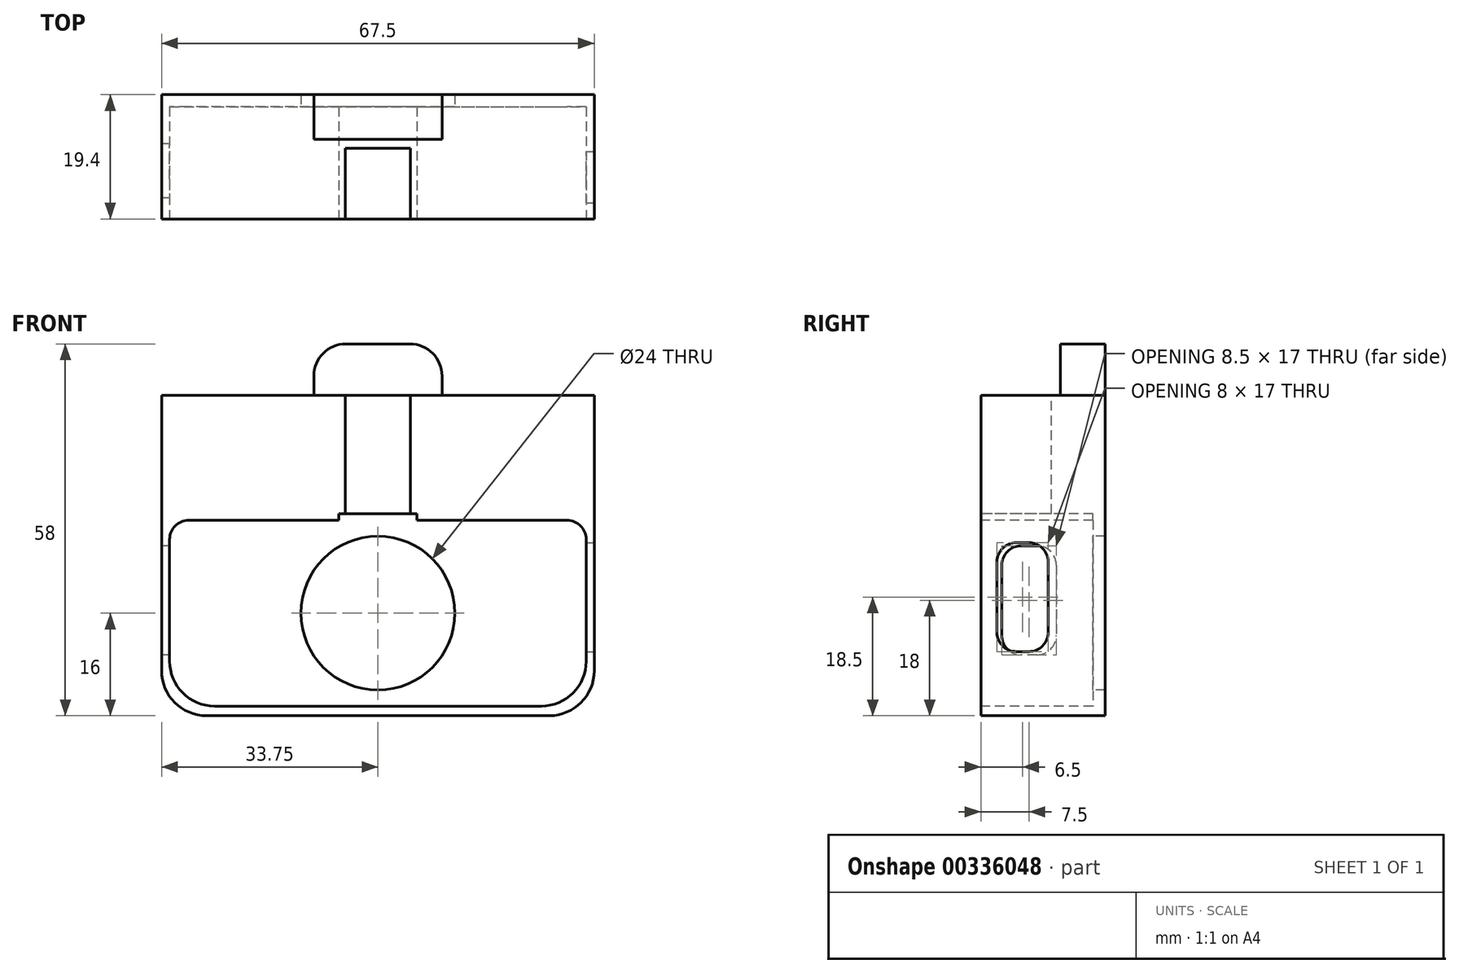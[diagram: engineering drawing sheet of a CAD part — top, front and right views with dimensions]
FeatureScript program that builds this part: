
annotation { "Feature Type Name" : "Feature", "Feature Type Description" : "" }
export const myFeature = defineFeature(function(context is Context, id is Id, definition is map)
    precondition{}
    {
        {
            var Q0;
            Q0=qCreatedBy(makeId("Top.planeOp"),FACE);
            var sketch = newSketch(context, id + "F0", { "sketchPlane" : qUnion([Q0])});
            skLineSegment(sketch, "E0.bottom", {"start": v(-33.75, 9.7) * mm, "end": v(33.75, 9.7) * mm});
            skLineSegment(sketch, "E0.top", {"start": v(-33.75, -9.7) * mm, "end": v(33.75, -9.7) * mm});
            skLineSegment(sketch, "E0.left", {"start": v(-33.75, 9.7) * mm, "end": v(-33.75, -9.7) * mm});
            skLineSegment(sketch, "E0.right", {"start": v(33.75, 9.7) * mm, "end": v(33.75, -9.7) * mm});
            skPoint(sketch, "E0.middle", {"position": v(0, 0) * mm});
            skSolve(sketch);
        }
        {
            var Q0;
            Q0=makeQuery(id+"F0.imprint","IMPRINT",FACE,{"disambiguationData":[TD([[makeQuery(id+"F0.imprint","IMPRINT",EDGE,{"derivedFrom":sQuery(id+"F0.wireOp",EDGE,"E0.bottom")}),-1.0]])]});
            extrude(context, id + "F1", {"entities" : qUnion([Q0]), "flatOperationType" : FlatOperationType.REMOVE, "offsetDistance" : 25 * mm, "depth" : 50 * mm, "domain" : OperationDomain.MODEL});
        }
        {
            var Q0;
            Q0=makeQuery(id+"F1.opExtrude","SWEPT_FACE",FACE,{"disambiguationData":[OSD([sQuery(id+"F0.wireOp",EDGE,"E0.top")])]});
            var sketch = newSketch(context, id + "F2", { "sketchPlane" : qUnion([Q0])});
            skLineSegment(sketch, "E1", {"start": v(-6.1, 30.5) * mm, "end": v(-29.5, 30.5) * mm});
            skLineSegment(sketch, "E2", {"start": v(-32.5, 27.5) * mm, "end": v(-32.5, 1.5) * mm});
            skLineSegment(sketch, "E3", {"start": v(-32.5, 1.5) * mm, "end": v(0, 1.5) * mm});
            skLineSegment(sketch, "E4.MirrorCS", {"start": v(6.1, 30.5) * mm, "end": v(29.5, 30.5) * mm});
            skLineSegment(sketch, "E5.MirrorCS", {"start": v(32.5, 27.5) * mm, "end": v(32.5, 1.5) * mm});
            skLineSegment(sketch, "E6.MirrorCS", {"start": v(32.5, 1.5) * mm, "end": v(0, 1.5) * mm});
            skPoint(sketch, "E7.visualSharp", {"position": v(-32.5, 30.5) * mm});
            skArc(sketch, "E7.filletArc", {"start": v(-29.5, 30.5) * mm, "mid": v(-31.62, 29.62) * mm, "end": v(-32.5, 27.5) * mm});
            skPoint(sketch, "E8.visualSharp", {"position": v(32.5, 30.5) * mm});
            skArc(sketch, "E8.filletArc", {"start": v(32.5, 27.5) * mm, "mid": v(31.62, 29.62) * mm, "end": v(29.5, 30.5) * mm});
            skLineSegment(sketch, "E9", {"start": v(-6.1, 30.5) * mm, "end": v(-6.1, 31.5) * mm});
            skLineSegment(sketch, "E10", {"start": v(-6.1, 31.5) * mm, "end": v(0, 31.5) * mm});
            skLineSegment(sketch, "E11.MirrorCS", {"start": v(6.1, 31.5) * mm, "end": v(0, 31.5) * mm});
            skLineSegment(sketch, "E12.MirrorCS", {"start": v(6.1, 30.5) * mm, "end": v(6.1, 31.5) * mm});
            skLineSegment(sketch, "E13", {"start": v(-5.1, 31.5) * mm, "end": v(-5.1, 50) * mm});
            skLineSegment(sketch, "E14", {"start": v(-5.1, 50) * mm, "end": v(0, 50) * mm});
            skLineSegment(sketch, "E15.MirrorCS", {"start": v(5.1, 50) * mm, "end": v(0, 50) * mm});
            skLineSegment(sketch, "E16.MirrorCS", {"start": v(5.1, 31.5) * mm, "end": v(5.1, 50) * mm});
            skSolve(sketch);
        }
        {
            var Q0;
            Q0=makeQuery(id+"F2.imprint","IMPRINT",FACE,{"disambiguationData":[TD([[makeQuery(id+"F2.imprint","IMPRINT",EDGE,{"derivedFrom":sQuery(id+"F2.wireOp",EDGE,"E1")}),1.0]])]});
            extrude(context, id + "F3", {"entities" : qUnion([Q0]), "operationType" : NewBodyOperationType.REMOVE, "flatOperationType" : FlatOperationType.REMOVE, "oppositeDirection" : true, "offsetDistance" : 25 * mm, "depth" : 17.5 * mm, "domain" : OperationDomain.MODEL});
        }
        {
            var Q0;
            Q0=makeQuery(id+"F3.boolean.opBoolean","COPY",FACE,{"derivedFrom":makeQuery(id+"F3.opExtrude","CAP_FACE",FACE,{"disambiguationData":[OSD([sQuery(id+"F2.wireOp",EDGE,"TUqootcI-8BxO-Xh3T-3ziC-AMeacjTwoGFO"),sQuery(id+"F2.wireOp",EDGE,"E1"),sQuery(id+"F2.wireOp",EDGE,"E2"),sQuery(id+"F2.wireOp",EDGE,"E3"),sQuery(id+"F2.wireOp",EDGE,"TnrEAHaC-nVOl-LSU4-eOLw-rkPotzCDHw9t"),sQuery(id+"F2.wireOp",EDGE,"8e3f61eb-42e3-43cc-a17b-0ce0254c29820.MirrorCS"),sQuery(id+"F2.wireOp",EDGE,"b324ff84-6e96-4d2f-b36d-c2ef43af87640.MirrorCS"),sQuery(id+"F2.wireOp",EDGE,"E4.MirrorCS"),sQuery(id+"F2.wireOp",EDGE,"E5.MirrorCS"),sQuery(id+"F2.wireOp",EDGE,"E6.MirrorCS")])],"isStart":false})});
            var sketch = newSketch(context, id + "F4", { "sketchPlane" : qUnion([Q0])});
            skCircle(sketch, "E17", {"center": v(0, 16) * mm, "radius": 12 * mm});
            skSolve(sketch);
        }
        {
            var Q0;
            Q0=makeQuery(id+"F4.imprint","IMPRINT",FACE,{"disambiguationData":[TD([[makeQuery(id+"F4.imprint","IMPRINT",EDGE,{"derivedFrom":sQuery(id+"F4.wireOp",EDGE,"E17")}),1.0]])]});
            extrude(context, id + "F5", {"entities" : qUnion([Q0]), "operationType" : NewBodyOperationType.REMOVE, "flatOperationType" : FlatOperationType.REMOVE, "endBound" : BoundingType.UP_TO_NEXT, "oppositeDirection" : true, "offsetDistance" : 25 * mm, "depth" : 25 * mm, "domain" : OperationDomain.MODEL});
        }
        {
            var Q0;
            Q0=makeQuery(id+"F1.opExtrude","SWEPT_FACE",FACE,{"disambiguationData":[OSD([sQuery(id+"F0.wireOp",EDGE,"E0.left")])]});
            var sketch = newSketch(context, id + "F6", { "sketchPlane" : qUnion([Q0])});
            skLineSegment(sketch, "E18.bottom", {"start": v(0.95, 26.5) * mm, "end": v(3.45, 26.5) * mm});
            skLineSegment(sketch, "E18.top", {"start": v(0.95, 9.5) * mm, "end": v(3.45, 9.5) * mm});
            skLineSegment(sketch, "E18.left", {"start": v(-2.05, 23.5) * mm, "end": v(-2.05, 12.5) * mm});
            skLineSegment(sketch, "E18.right", {"start": v(6.45, 23.5) * mm, "end": v(6.45, 12.5) * mm});
            skPoint(sketch, "E18.middle", {"position": v(2.2, 18) * mm});
            skPoint(sketch, "E19.visualSharp", {"position": v(-2.05, 9.5) * mm});
            skArc(sketch, "E19.filletArc", {"start": v(-2.05, 12.5) * mm, "mid": v(-1.17, 10.38) * mm, "end": v(0.95, 9.5) * mm});
            skPoint(sketch, "E20.visualSharp", {"position": v(-2.05, 26.5) * mm});
            skArc(sketch, "E20.filletArc", {"start": v(0.95, 26.5) * mm, "mid": v(-1.17, 25.62) * mm, "end": v(-2.05, 23.5) * mm});
            skPoint(sketch, "E21.visualSharp", {"position": v(6.45, 26.5) * mm});
            skArc(sketch, "E21.filletArc", {"start": v(6.45, 23.5) * mm, "mid": v(5.57, 25.62) * mm, "end": v(3.45, 26.5) * mm});
            skPoint(sketch, "E22.visualSharp", {"position": v(6.45, 9.5) * mm});
            skArc(sketch, "E22.filletArc", {"start": v(3.45, 9.5) * mm, "mid": v(5.57, 10.38) * mm, "end": v(6.45, 12.5) * mm});
            skSolve(sketch);
        }
        {
            var Q0;
            Q0=makeQuery(id+"F6.imprint","IMPRINT",FACE,{"disambiguationData":[TD([[makeQuery(id+"F6.imprint","IMPRINT",EDGE,{"derivedFrom":sQuery(id+"F6.wireOp",EDGE,"E18.bottom")}),-1.0]])]});
            extrude(context, id + "F7", {"entities" : qUnion([Q0]), "operationType" : NewBodyOperationType.REMOVE, "endBound" : BoundingType.UP_TO_NEXT, "oppositeDirection" : true, "depth" : 25 * mm});
        }
        {
            var Q0;
            {var subQ0=sQuery(id+"F2.wireOp",EDGE,"E13");Q0=makeQuery(id+"F2.imprint","IMPRINT",FACE,{"disambiguationData":[TD([[makeQuery(id+"F2.imprint","IMPRINT",EDGE,{"derivedFrom":subQ0}),-1.0]])]});}
            extrude(context, id + "F8", {"entities" : qUnion([Q0]), "operationType" : NewBodyOperationType.REMOVE, "oppositeDirection" : true, "depth" : 11 * mm});
        }
        {
            var Q0;
            Q0=makeQuery(id+"F3.boolean.opBoolean","COPY",EDGE,{"derivedFrom":makeQuery(id+"F3.opExtrude","SWEPT_EDGE",EDGE,{"disambiguationData":[OSD([sQuery(id+"F2.wireOp",EDGE,"E5.MirrorCS"),sQuery(id+"F2.wireOp",EDGE,"E6.MirrorCS")])]})});
            var Q1;
            Q1=makeQuery(id+"F1.opExtrude","CAP_EDGE",EDGE,{"disambiguationData":[OSD([sQuery(id+"F0.wireOp",EDGE,"E0.left")])],"isStart":true});
            var Q2;
            Q2=makeQuery(id+"F3.boolean.opBoolean","COPY",EDGE,{"derivedFrom":makeQuery(id+"F3.opExtrude","SWEPT_EDGE",EDGE,{"disambiguationData":[OSD([sQuery(id+"F2.wireOp",EDGE,"E2"),sQuery(id+"F2.wireOp",EDGE,"E3")])]})});
            var Q3;
            Q3=makeQuery(id+"F1.opExtrude","CAP_EDGE",EDGE,{"disambiguationData":[OSD([sQuery(id+"F0.wireOp",EDGE,"E0.right")])],"isStart":true});
            fillet(context, id + "F9", {"entities" : qUnion([Q0, Q1, Q2, Q3]), "radius" : 7 * mm, "tangentPropagation" : true, "allowEdgeOverflow" : false});
        }
        {
            var Q0;
            Q0=makeQuery(id+"F1.opExtrude","CAP_FACE",FACE,{"disambiguationData":[OSD([sQuery(id+"F0.wireOp",EDGE,"E0.bottom"),sQuery(id+"F0.wireOp",EDGE,"E0.top"),sQuery(id+"F0.wireOp",EDGE,"E0.left"),sQuery(id+"F0.wireOp",EDGE,"E0.right")])],"isStart":false});
            var sketch = newSketch(context, id + "F10", { "sketchPlane" : qUnion([Q0])});
            skLineSegment(sketch, "E23", {"start": v(0, 9.7) * mm, "end": v(-10, 9.7) * mm});
            skLineSegment(sketch, "E24", {"start": v(-10, 9.7) * mm, "end": v(-10, 2.7) * mm});
            skLineSegment(sketch, "E25", {"start": v(-10, 2.7) * mm, "end": v(0, 2.7) * mm});
            skLineSegment(sketch, "E26.MirrorCS", {"start": v(0, 9.7) * mm, "end": v(10, 9.7) * mm});
            skLineSegment(sketch, "E27.MirrorCS", {"start": v(10, 9.7) * mm, "end": v(10, 2.7) * mm});
            skLineSegment(sketch, "E28.MirrorCS", {"start": v(10, 2.7) * mm, "end": v(0, 2.7) * mm});
            skSolve(sketch);
        }
        {
            var Q0;
            Q0=makeQuery(id+"F10.imprint","IMPRINT",FACE,{"disambiguationData":[TD([[makeQuery(id+"F10.imprint","IMPRINT",EDGE,{"derivedFrom":sQuery(id+"F10.wireOp",EDGE,"E23")}),-1.0]])]});
            extrude(context, id + "F11", {"entities" : qUnion([Q0]), "operationType" : NewBodyOperationType.ADD, "depth" : 8 * mm});
        }
        {
            var Q0;
            Q0=makeQuery(id+"F11.opExtrude","CAP_EDGE",EDGE,{"disambiguationData":[OSD([sQuery(id+"F10.wireOp",EDGE,"E27.MirrorCS")])],"isStart":false});
            var Q1;
            Q1=makeQuery(id+"F11.opExtrude","CAP_EDGE",EDGE,{"disambiguationData":[OSD([sQuery(id+"F10.wireOp",EDGE,"E24")])],"isStart":false});
            fillet(context, id + "F12", {"entities" : qUnion([Q0, Q1]), "radius" : 5 * mm, "tangentPropagation" : true, "allowEdgeOverflow" : false});
        }
        {
            var Q0;
            Q0=makeQuery(id+"F1.opExtrude","SWEPT_FACE",FACE,{"disambiguationData":[OSD([sQuery(id+"F0.wireOp",EDGE,"E0.right")])]});
            var sketch = newSketch(context, id + "F13", { "sketchPlane" : qUnion([Q0])});
            skLineSegment(sketch, "E29.bottom", {"start": v(-4.2, 27) * mm, "end": v(-2.2, 27) * mm});
            skLineSegment(sketch, "E29.top", {"start": v(-4.2, 10) * mm, "end": v(-2.2, 10) * mm});
            skLineSegment(sketch, "E29.left", {"start": v(-7.2, 24) * mm, "end": v(-7.2, 13) * mm});
            skLineSegment(sketch, "E29.right", {"start": v(0.8, 24) * mm, "end": v(0.8, 13) * mm});
            skPoint(sketch, "E29.middle", {"position": v(-3.2, 18.5) * mm});
            skPoint(sketch, "E30.visualSharp", {"position": v(-7.2, 27) * mm});
            skArc(sketch, "E30.filletArc", {"start": v(-4.2, 27) * mm, "mid": v(-6.32, 26.12) * mm, "end": v(-7.2, 24) * mm});
            skPoint(sketch, "E31.visualSharp", {"position": v(0.8, 27) * mm});
            skArc(sketch, "E31.filletArc", {"start": v(0.8, 24) * mm, "mid": v(-0.08, 26.12) * mm, "end": v(-2.2, 27) * mm});
            skPoint(sketch, "E32.visualSharp", {"position": v(0.8, 10) * mm});
            skArc(sketch, "E32.filletArc", {"start": v(-2.2, 10) * mm, "mid": v(-0.08, 10.88) * mm, "end": v(0.8, 13) * mm});
            skPoint(sketch, "E33.visualSharp", {"position": v(-7.2, 10) * mm});
            skArc(sketch, "E33.filletArc", {"start": v(-7.2, 13) * mm, "mid": v(-6.32, 10.88) * mm, "end": v(-4.2, 10) * mm});
            skSolve(sketch);
        }
        {
            var Q0;
            Q0=makeQuery(id+"F13.imprint","IMPRINT",FACE,{"disambiguationData":[TD([[makeQuery(id+"F13.imprint","IMPRINT",EDGE,{"derivedFrom":sQuery(id+"F13.wireOp",EDGE,"E29.bottom")}),-1.0]])]});
            extrude(context, id + "F14", {"entities" : qUnion([Q0]), "operationType" : NewBodyOperationType.REMOVE, "endBound" : BoundingType.UP_TO_NEXT, "oppositeDirection" : true, "depth" : 25 * mm});
        }
    });
